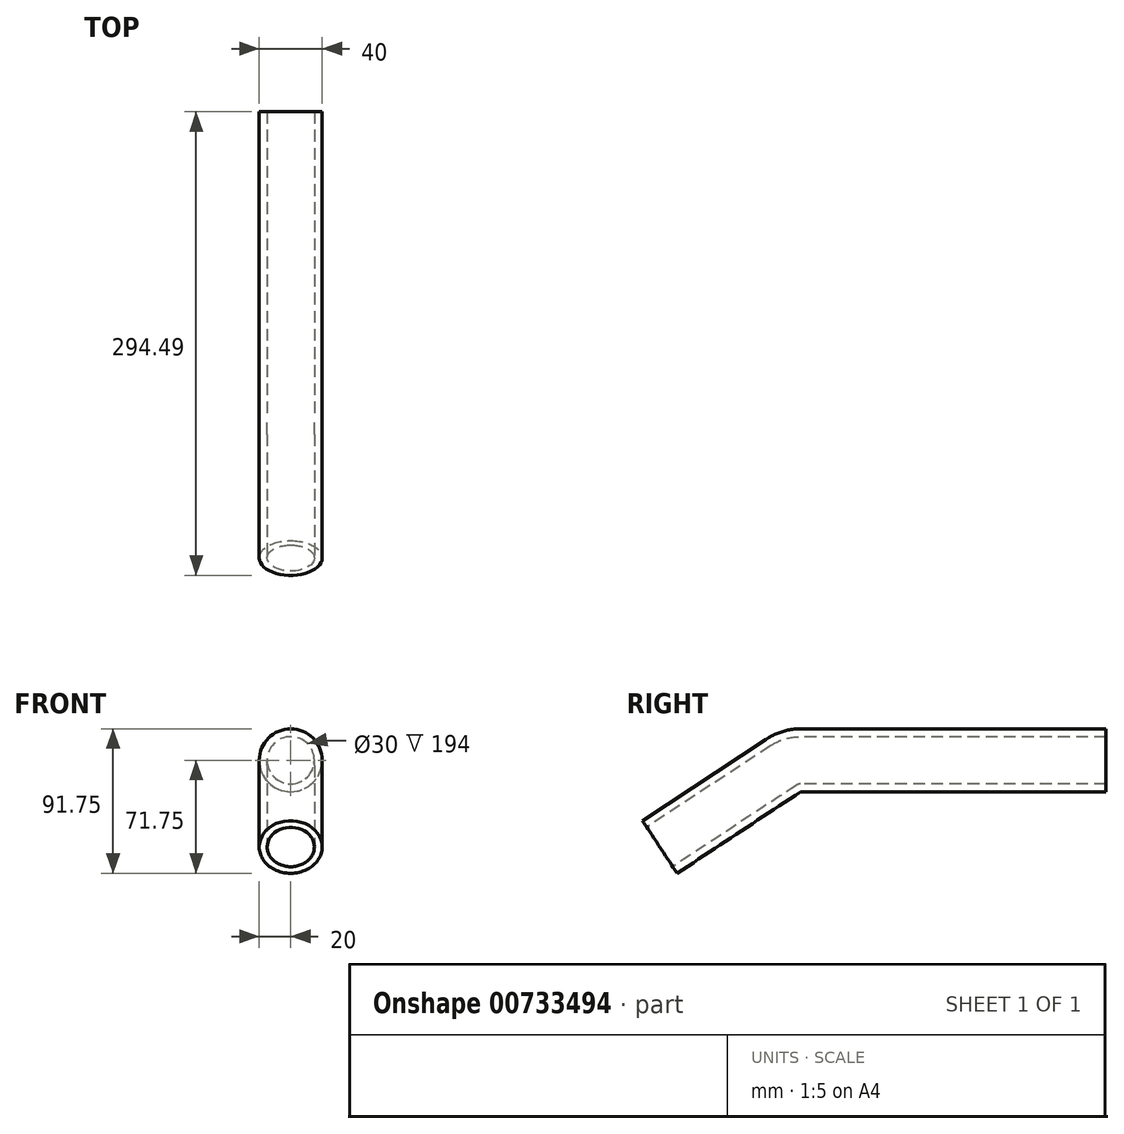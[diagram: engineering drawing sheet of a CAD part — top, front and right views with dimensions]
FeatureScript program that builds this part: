
annotation { "Feature Type Name" : "Feature", "Feature Type Description" : "" }
export const myFeature = defineFeature(function(context is Context, id is Id, definition is map)
    precondition{}
    {
        {
            var Q0;
            Q0=qCreatedBy(makeId("Right.planeOp"),FACE);
            var sketch = newSketch(context, id + "F0", { "sketchPlane" : qUnion([Q0])});
            skLineSegment(sketch, "E0", {"start": v(6, 0) * mm, "end": v(200, 0) * mm});
            skLineSegment(sketch, "E1", {"start": v(-5, -3.3) * mm, "end": v(-83.48, -55.05) * mm});
            skPoint(sketch, "E2.visualSharp", {"position": v(0, 0) * mm});
            skArc(sketch, "E2.filletArc", {"start": v(6, 0) * mm, "mid": v(0.25, -0.84) * mm, "end": v(-5, -3.3) * mm});
            skSolve(sketch);
        }
        {
            var Q0;
            Q0=qCreatedBy(makeId("Front.planeOp"),FACE);
            cPlane(context, id + "F1", {"entities" : qUnion([Q0]), "cplaneType" : CPlaneType.OFFSET, "offset" : 200 * mm, "oppositeDirection" : true, "width" : 150 * mm, "height" : 150 * mm});
        }
        {
            var Q0;
            Q0=qCreatedBy(id+"F1.planeOp",FACE);
            var sketch = newSketch(context, id + "F2", { "sketchPlane" : qUnion([Q0])});
            skCircle(sketch, "E3", {"center": v(0, 0) * mm, "radius": 15 * mm});
            skCircle(sketch, "E4", {"center": v(0, 0) * mm, "radius": 20 * mm});
            skSolve(sketch);
        }
        {
            var Q0;
            Q0=makeQuery(id+"F2.imprint","IMPRINT",FACE,{"disambiguationData":[TD([[makeQuery(id+"F2.imprint","IMPRINT",EDGE,{"derivedFrom":sQuery(id+"F2.wireOp",EDGE,"E3")}),-1.0]])]});
            var Q1;
            Q1=sQuery(id+"F0.wireOp",EDGE,"E0");
            var Q2;
            Q2=sQuery(id+"F0.wireOp",EDGE,"E2.filletArc");
            var Q3;
            Q3=sQuery(id+"F0.wireOp",EDGE,"E1");
            sweep(context, id + "F3", {"profiles" : qUnion([Q0]), "path" : qUnion([Q1, Q2, Q3])});
        }
    });
